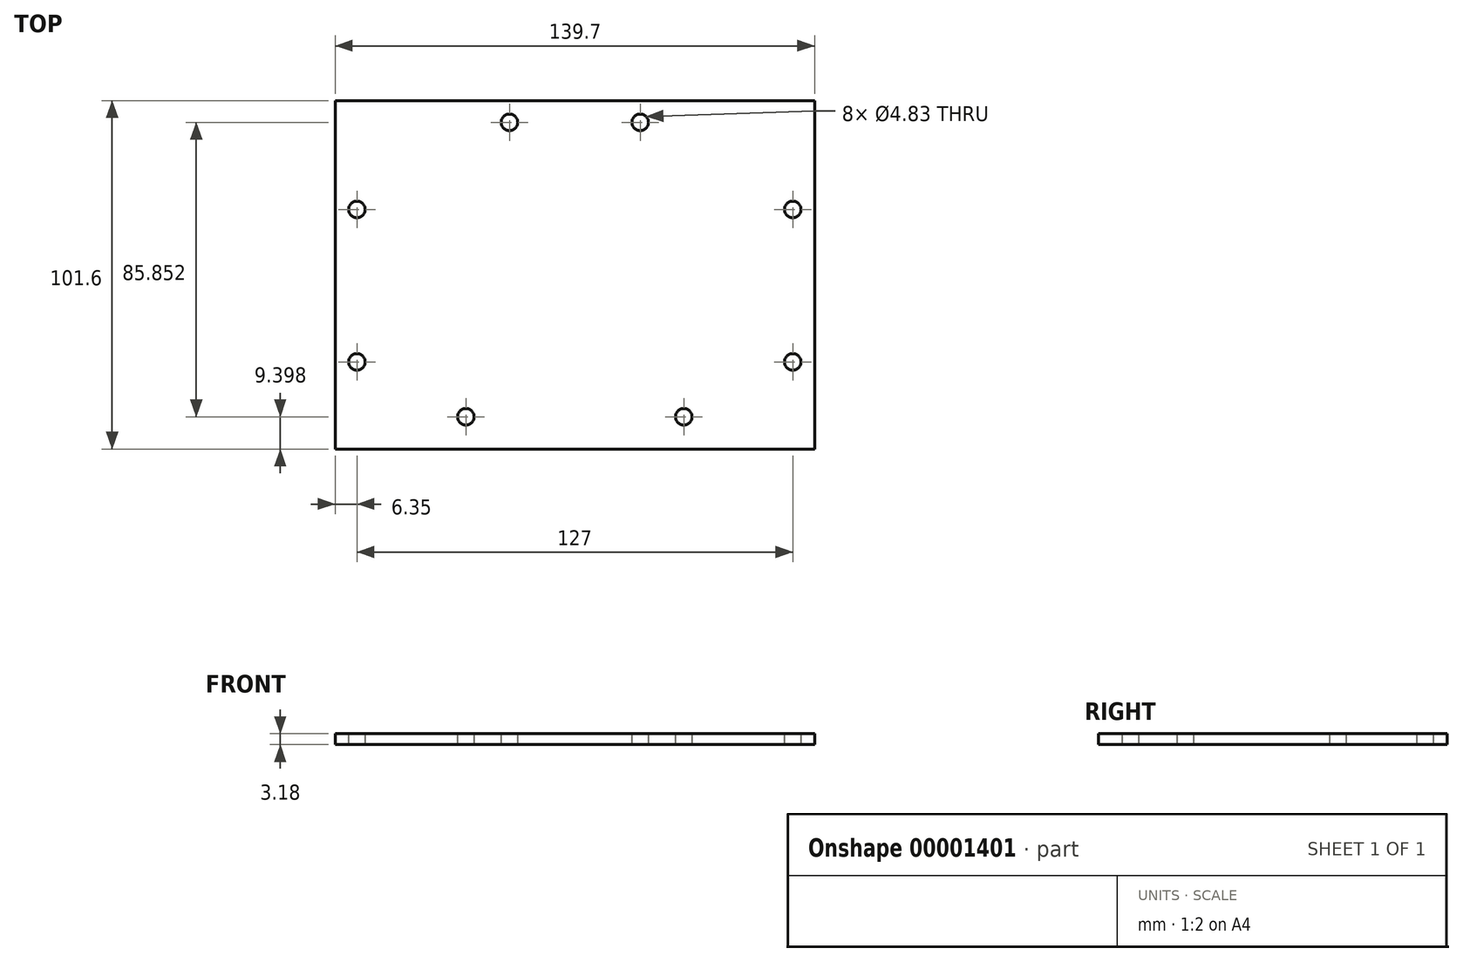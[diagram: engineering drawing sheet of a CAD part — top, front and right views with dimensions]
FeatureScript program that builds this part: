
annotation { "Feature Type Name" : "Feature", "Feature Type Description" : "" }
export const myFeature = defineFeature(function(context is Context, id is Id, definition is map)
    precondition{}
    {
        {
            var Q0;
            Q0=qCreatedBy(makeId("Top.planeOp"),FACE);
            var sketch = newSketch(context, id + "F0", { "sketchPlane" : qUnion([Q0])});
            skLineSegment(sketch, "E0.rect.bottom", {"start": v(69.85, 50.8) * mm, "end": v(-69.85, 50.8) * mm});
            skLineSegment(sketch, "E0.rect.top", {"start": v(69.85, -50.8) * mm, "end": v(-69.85, -50.8) * mm});
            skLineSegment(sketch, "E0.rect.left", {"start": v(69.85, 50.8) * mm, "end": v(69.85, -50.8) * mm});
            skLineSegment(sketch, "E0.rect.right", {"start": v(-69.85, 50.8) * mm, "end": v(-69.85, -50.8) * mm});
            skPoint(sketch, "E0.rect.middle", {"position": v(0, 0) * mm});
            skSolve(sketch);
        }
        {
            var Q0;
            Q0 = qSketchRegion(id + "F0", true);
            extrude(context, id + "F1", {"entities" : qUnion([Q0]), "endBound" : BoundingType.SYMMETRIC, "depth" : 3.17 * mm});
        }
        {
            var Q0;
            Q0=makeQuery(id+"F1.opExtrude","CAP_FACE",FACE,{"disambiguationData":[OSD([sQuery(id+"F0.wireOp",EDGE,"E0.rect.bottom"),sQuery(id+"F0.wireOp",EDGE,"E0.rect.top"),sQuery(id+"F0.wireOp",EDGE,"E0.rect.left"),sQuery(id+"F0.wireOp",EDGE,"E0.rect.right")])],"isStart":false});
            var sketch = newSketch(context, id + "F2", { "sketchPlane" : qUnion([Q0])});
            skCircle(sketch, "E1", {"center": v(-19.05, 44.45) * mm, "radius": 2.41 * mm});
            skCircle(sketch, "E2", {"center": v(19.05, 44.45) * mm, "radius": 2.41 * mm});
            skCircle(sketch, "E3", {"center": v(63.5, 19.05) * mm, "radius": 2.41 * mm});
            skCircle(sketch, "E4", {"center": v(63.5, -25.4) * mm, "radius": 2.41 * mm});
            skCircle(sketch, "E5", {"center": v(31.75, -41.4) * mm, "radius": 2.41 * mm});
            skCircle(sketch, "E6", {"center": v(-31.75, -41.4) * mm, "radius": 2.41 * mm});
            skCircle(sketch, "E7", {"center": v(-63.5, -25.4) * mm, "radius": 2.41 * mm});
            skCircle(sketch, "E8", {"center": v(-63.5, 19.05) * mm, "radius": 2.41 * mm});
            skSolve(sketch);
        }
        {
            var Q0;
            Q0 = qSketchRegion(id + "F2", true);
            extrude(context, id + "F3", {"entities" : qUnion([Q0]), "operationType" : NewBodyOperationType.REMOVE, "endBound" : BoundingType.THROUGH_ALL, "oppositeDirection" : true, "depth" : 25.4 * mm});
        }
    });
